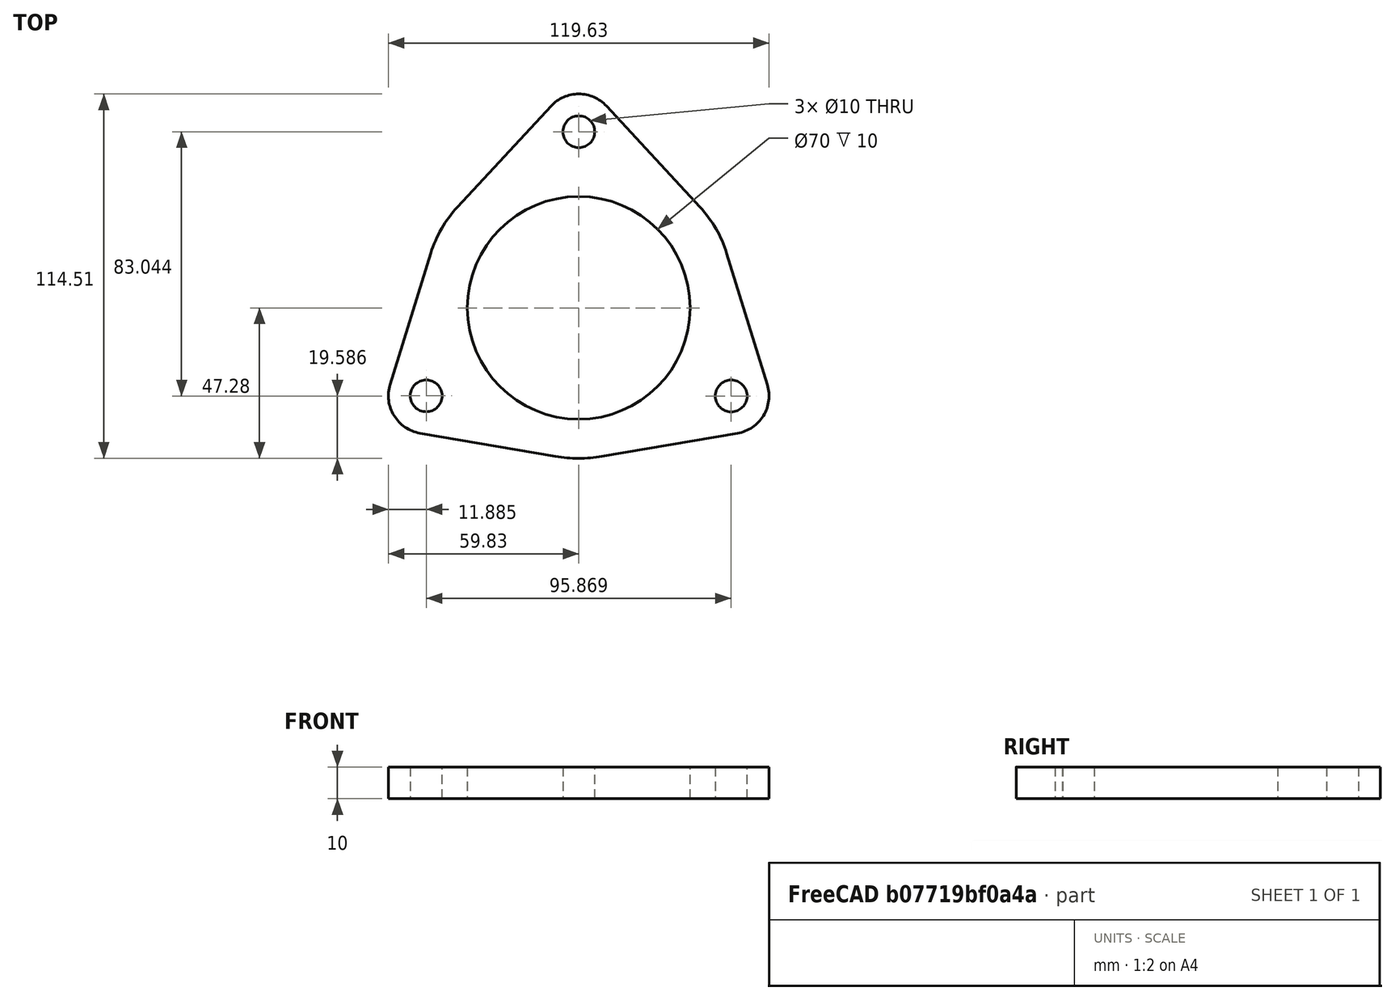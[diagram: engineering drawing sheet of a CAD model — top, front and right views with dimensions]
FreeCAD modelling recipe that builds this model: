
FCSTD DOCUMENT  (FreeCAD 1.0R39319 (Git))
Label: tutor_3
License: All rights reserved
LicenseURL: https://en.wikipedia.org/wiki/All_rights_reserved
objects: Image::ImagePlane×1, Sketcher::SketchObject×1, PartDesign::Pad×1, PartDesign::Body×1
note: 6 computed .brp shape members not serialized (recipe doc carries the construction recipe); baked Part::Feature solids carry a one-line shape summary decoded from their .brp

FEATURE [Image::ImagePlane] gasketflange1
  Placement = pos=(0,10,0) rot=(0,0,1;0rad)
  XSize = 120
  YSize = 115
FEATURE [Sketcher::SketchObject] Sketch
  ArcFitTolerance = 1e-06
  FullyConstrained = false
  MakeInternals = false
  sketch-geometry (19):
    g0: Circle CenterX=0 CenterY=0 CenterZ=0 NormalX=0 NormalY=0 NormalZ=1 AngleXU=0 Radius=35
    g1: Circle CenterX=-47.9453 CenterY=-27.6563 CenterZ=0 NormalX=0 NormalY=0 NormalZ=1 AngleXU=0 Radius=5
    g2: LineSegment [constr] StartX=0 StartY=0 StartZ=0 EndX=-47.9453 EndY=-27.6563 EndZ=0
    g3: Circle CenterX=47.9237 CenterY=-27.6937 CenterZ=0 NormalX=0 NormalY=0 NormalZ=1 AngleXU=0 Radius=5
    g4: LineSegment [constr] StartX=0 StartY=0 StartZ=0 EndX=47.9237 EndY=-27.6937 EndZ=0
    g5: Circle CenterX=0.02158 CenterY=55.35 CenterZ=0 NormalX=0 NormalY=0 NormalZ=1 AngleXU=0 Radius=5
    g6: LineSegment [constr] StartX=0.02158 StartY=55.35 StartZ=0 EndX=0 EndY=0 EndZ=0
    g7: ArcOfCircle CenterX=0.02158 CenterY=55.35 CenterZ=0 NormalX=0 NormalY=0 NormalZ=1 AngleXU=0 Radius=11.88 StartAngle=0.746929 EndAngle=2.39388
    g8: LineSegment StartX=8.73887 StartY=63.4211 StartZ=0 EndX=38.1224 EndY=31.6852 EndZ=0
    g9: ArcOfCircle CenterX=10.3467 CenterY=5.96827 CenterZ=0 NormalX=0 NormalY=0 NormalZ=1 AngleXU=0 Radius=37.8531 StartAngle=0.299489 EndAngle=0.746929
    g10: ArcOfCircle CenterX=47.9237 CenterY=-27.6937 CenterZ=0 NormalX=0 NormalY=0 NormalZ=1 AngleXU=0 Radius=11.88 StartAngle=4.88112 EndAngle=6.58267
    g11: LineSegment StartX=46.5148 StartY=17.1361 StartZ=0 EndX=59.2749 EndY=-24.1887 EndZ=0
    g12: ArcOfCircle CenterX=-47.9453 CenterY=-27.6563 CenterZ=0 NormalX=0 NormalY=0 NormalZ=1 AngleXU=0 Radius=11.88 StartAngle=2.84132 EndAngle=4.54288
    g13: LineSegment StartX=49.9187 StartY=-39.405 StartZ=0 EndX=7.28291 EndY=-46.6679 EndZ=0
    g14: ArcOfCircle CenterX=-0.0015229 CenterY=-3.90604 CenterZ=0 NormalX=0 NormalY=0 NormalZ=1 AngleXU=0 Radius=43.3779 StartAngle=4.54288 EndAngle=4.88112
    g15: LineSegment StartX=-49.9494 StartY=-39.366 StartZ=0 EndX=-7.3193 EndY=-46.6622 EndZ=0
    g16: LineSegment StartX=-59.2938 StartY=-24.1425 StartZ=0 EndX=-46.5014 EndY=17.1724 EndZ=0
    g17: ArcOfCircle CenterX=-10.342 CenterY=5.97633 CenterZ=0 NormalX=0 NormalY=0 NormalZ=1 AngleXU=0 Radius=37.8531 StartAngle=2.39388 EndAngle=2.84132
    g18: LineSegment StartX=-8.68941 StartY=63.4279 StartZ=0 EndX=-38.0977 EndY=31.7149 EndZ=0
  constraints (41):
    c: Diameter(g0) = 70
    c: Coincident(g0,g-1)
    c: Diameter(g1) = 10
    c: Coincident(g2,g0)
    c: Coincident(g2,g1)
    c: Coincident(g4,g0)
    c: Coincident(g4,g3)
    c: Angle(g2,g4) = 2.0944
    c: Equal(g3,g1)
    c: Equal(g2,g4)
    c: Coincident(g6,g5)
    c: Coincident(g6,g0)
    c: Angle(g4,g6) = 2.0944
    c: Equal(g4,g6)
    c: Equal(g5,g3)
    c: DistanceY(g6,g6) = 55.35
    c: Coincident(g7,g5)
    c: Coincident(g10,g3)
    c: Coincident(g12,g1)
    c: Diameter(g7) = 23.76
    c: Equal(g7,g10)
    c: Equal(g10,g12)
    c: Tangent(g8,g7) = 1.5708
    c: Tangent(g9,g8) = 1.5708
    c: Tangent(g11,g9) = 1.5708
    c: Tangent(g11,g10) = 1.5708
    c: Tangent(g13,g10) = 1.5708
    c: Tangent(g14,g13) = 1.5708
    c: Tangent(g15,g14) = -1.5708
    c: Tangent(g15,g12) = -1.5708
    c: Tangent(g18,g17) = -1.5708
    c: Tangent(g17,g16) = 1.5708
    c: Tangent(g18,g7) = -1.5708
    c: Tangent(g16,g12) = 1.5708
    c: Equal(g8,g18)
    c: Equal(g18,g16)
    c: Equal(g16,g11)
    c: Equal(g11,g13)
    c: Equal(g13,g15)
    c: Equal(g9,g17)
    c: Distance(g8) = 43.25
FEATURE [PartDesign::Pad] Pad
  Direction = (0,0,1)
  Length = 10
  Length2 = 10
  Profile = -> Sketch
  ReferenceAxis = -> Sketch [N_Axis]
  Refine = true
  Suppressed = false
  Type = 0
FEATURE [PartDesign::Body] Body
  AllowCompound = false
  Group = -> [Sketch,Pad]
  Origin = -> Origin
  Tip = -> Pad
